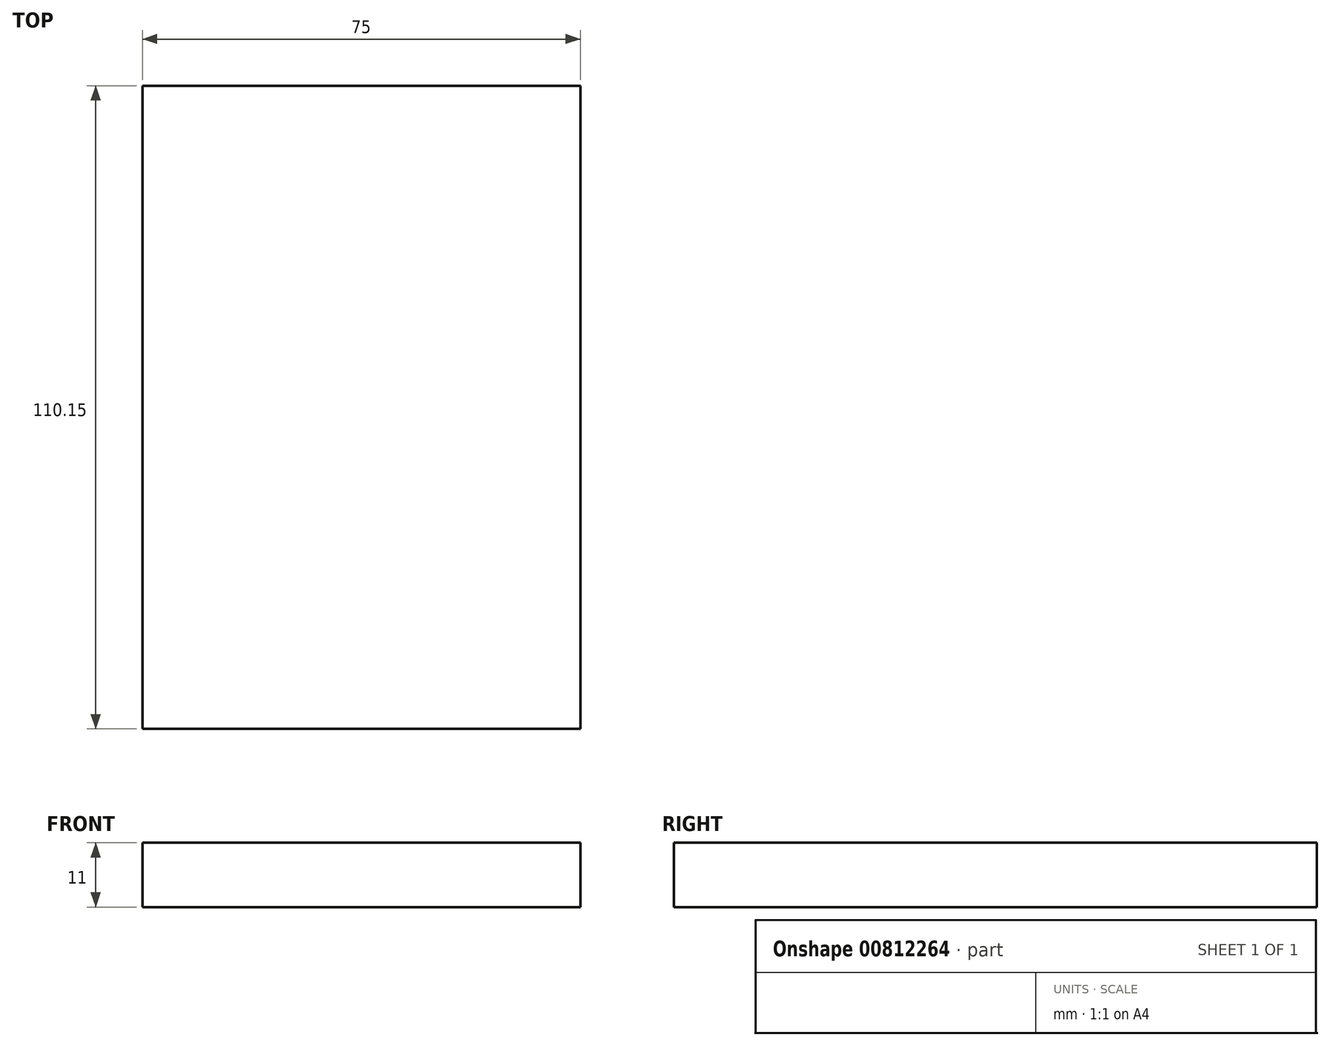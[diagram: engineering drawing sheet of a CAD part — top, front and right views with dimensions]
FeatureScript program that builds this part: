
annotation { "Feature Type Name" : "Feature", "Feature Type Description" : "" }
export const myFeature = defineFeature(function(context is Context, id is Id, definition is map)
    precondition{}
    {
        {
            var Q0;
            Q0=qCreatedBy(makeId("Top.planeOp"),FACE);
            var sketch = newSketch(context, id + "F0", { "sketchPlane" : qUnion([Q0])});
            skLineSegment(sketch, "E0", {"start": v(-37.35, -28.95) * mm, "end": v(37.65, -28.95) * mm});
            skLineSegment(sketch, "E1", {"start": v(37.65, 81.2) * mm, "end": v(-37.35, 81.2) * mm});
            skLineSegment(sketch, "E2", {"start": v(-37.35, 81.2) * mm, "end": v(-37.35, -28.95) * mm});
            skLineSegment(sketch, "E3", {"start": v(37.65, -28.95) * mm, "end": v(37.65, 81.2) * mm});
            skSolve(sketch);
        }
        {
            var Q0;
            Q0=qSketchRegion(id+"F0",true);
            extrude(context, id + "F1", {"entities" : qUnion([Q0]), "depth" : 11 * mm, "offsetDistance" : 25 * mm});
        }
    });
